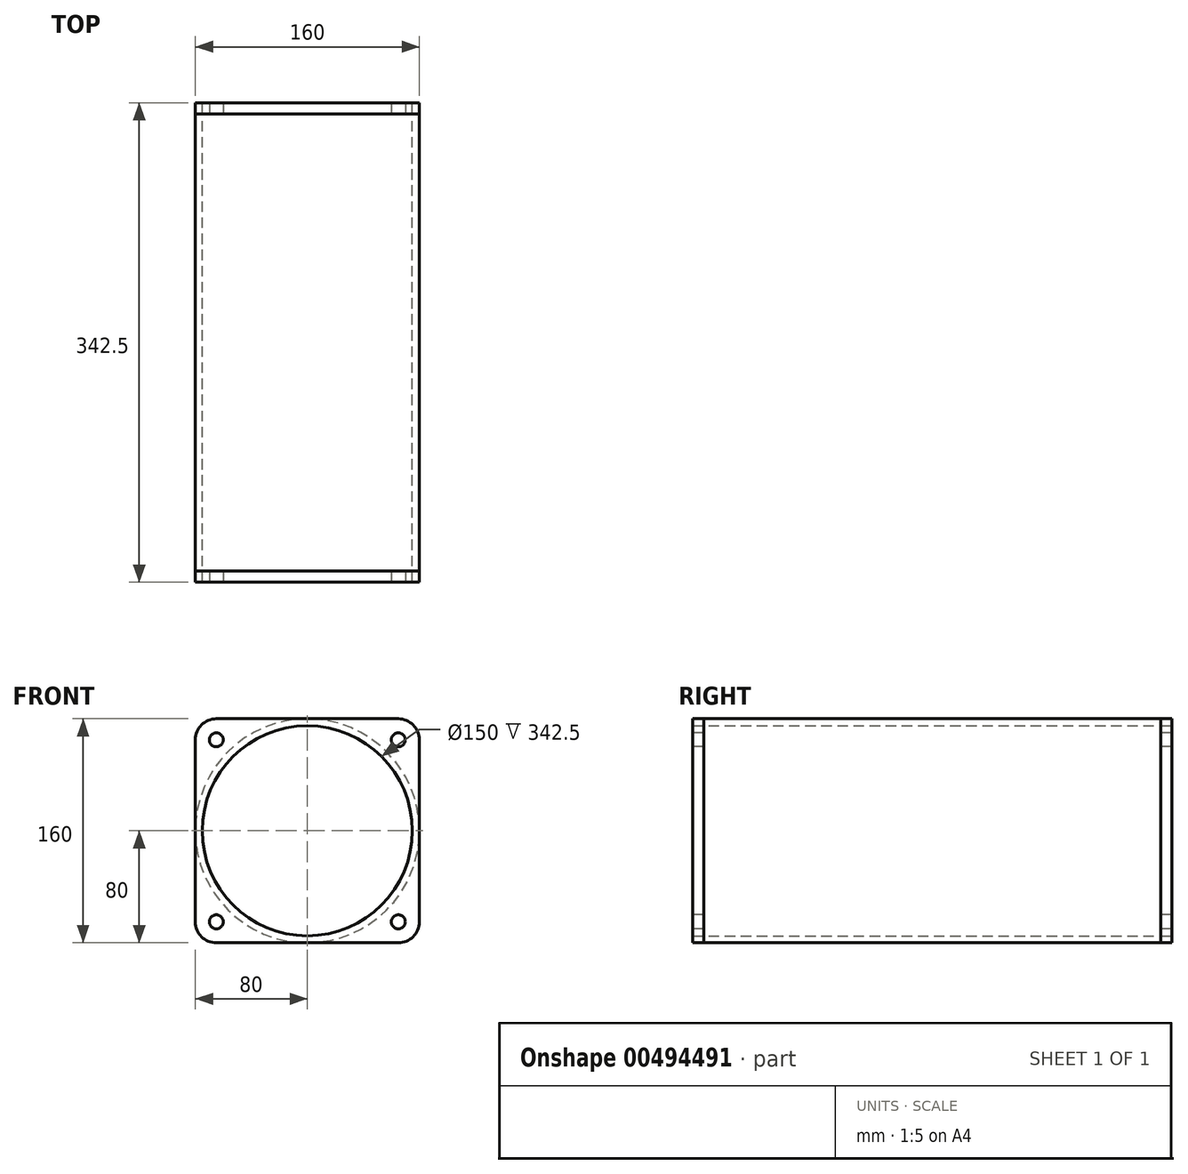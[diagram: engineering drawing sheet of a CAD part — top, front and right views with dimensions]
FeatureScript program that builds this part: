
annotation { "Feature Type Name" : "Feature", "Feature Type Description" : "" }
export const myFeature = defineFeature(function(context is Context, id is Id, definition is map)
    precondition{}
    {
        {
            var Q0;
            Q0=qCreatedBy(makeId("Front.planeOp"),FACE);
            var sketch = newSketch(context, id + "F0", { "sketchPlane" : qUnion([Q0])});
            skLineSegment(sketch, "E0.bottom", {"start": v(80, -80) * mm, "end": v(-80, -80) * mm});
            skLineSegment(sketch, "E0.top", {"start": v(80, 80) * mm, "end": v(-80, 80) * mm});
            skLineSegment(sketch, "E0.left", {"start": v(80, -80) * mm, "end": v(80, 80) * mm});
            skLineSegment(sketch, "E0.right", {"start": v(-80, -80) * mm, "end": v(-80, 80) * mm});
            skPoint(sketch, "E0.middle", {"position": v(0, 0) * mm});
            skCircle(sketch, "E1", {"center": v(0, 0) * mm, "radius": 75 * mm});
            skSolve(sketch);
        }
        {
            var Q0;
            Q0=makeQuery(id+"F0.imprint","IMPRINT",FACE,{"disambiguationData":[TD([[makeQuery(id+"F0.imprint","IMPRINT",EDGE,{"derivedFrom":sQuery(id+"F0.wireOp",EDGE,"E1")}),1.0]])]});
            extrude(context, id + "F1", {"entities" : qUnion([Q0]), "endBound" : BoundingType.SYMMETRIC, "depth" : 342.5 * mm});
        }
        {
            var Q0;
            Q0=makeQuery(id+"F1.opExtrude","CAP_FACE",FACE,{"disambiguationData":[OSD([sQuery(id+"F0.wireOp",EDGE,"E1")])],"isStart":false});
            var Q1;
            Q1=makeQuery(id+"F1.opExtrude","CAP_FACE",FACE,{"disambiguationData":[OSD([sQuery(id+"F0.wireOp",EDGE,"E1")])],"isStart":true});
            shell(context, id + "F2", {"entities" : qUnion([Q0, Q1]), "thickness" : 5 * mm, "oppositeDirection" : true});
        }
        {
            var Q0;
            Q0 = qSketchRegion(id + "F0", true);
            extrude(context, id + "F3", {"entities" : qUnion([Q0]), "operationType" : NewBodyOperationType.ADD, "oppositeDirection" : true, "depth" : (342.5 / 2) * mm, "hasSecondDirection" : true, "secondDirectionOppositeDirection" : true, "secondDirectionDepth" : (342.5 / 2 - 8) * mm});
        }
        {
            var Q0;
            Q0 = qSketchRegion(id + "F0", true);
            extrude(context, id + "F4", {"entities" : qUnion([Q0]), "operationType" : NewBodyOperationType.ADD, "depth" : (342.5 / 2) * mm, "hasSecondDirection" : true, "secondDirectionOppositeDirection" : false, "secondDirectionDepth" : (342.5 / 2 - 8) * mm});
        }
        {
            var Q0;
            {var subQ0=sQuery(id+"F0.wireOp",EDGE,"E1");Q0=makeQuery(id+"F4.boolean.opBoolean","MERGE",FACE,{"derivedFrom":[makeQuery(id+"F1.opExtrude","CAP_FACE",FACE,{"disambiguationData":[OSD([subQ0])],"isStart":false}),makeQuery(id+"F4.opExtrude","CAP_FACE",FACE,{"disambiguationData":[OSD([sQuery(id+"F0.wireOp",EDGE,"E0.bottom"),sQuery(id+"F0.wireOp",EDGE,"E0.top"),sQuery(id+"F0.wireOp",EDGE,"E0.left"),sQuery(id+"F0.wireOp",EDGE,"E0.right"),subQ0])],"isStart":false})]});}
            var sketch = newSketch(context, id + "F5", { "sketchPlane" : qUnion([Q0])});
            skCircle(sketch, "E2", {"center": v(-65, 65) * mm, "radius": 5 * mm});
            skCircle(sketch, "E3", {"center": v(65, 65) * mm, "radius": 5 * mm});
            skCircle(sketch, "E4", {"center": v(65, -65) * mm, "radius": 5 * mm});
            skCircle(sketch, "E5", {"center": v(-65, -65) * mm, "radius": 5 * mm});
            skSolve(sketch);
        }
        {
            var Q0;
            Q0=makeQuery(id+"F5.imprint","IMPRINT",FACE,{"disambiguationData":[TD([[makeQuery(id+"F5.imprint","IMPRINT",EDGE,{"derivedFrom":sQuery(id+"F5.wireOp",EDGE,"E2")}),1.0]])]});
            var Q1;
            Q1=makeQuery(id+"F5.imprint","IMPRINT",FACE,{"disambiguationData":[TD([[makeQuery(id+"F5.imprint","IMPRINT",EDGE,{"derivedFrom":sQuery(id+"F5.wireOp",EDGE,"E3")}),1.0]])]});
            var Q2;
            Q2=makeQuery(id+"F5.imprint","IMPRINT",FACE,{"disambiguationData":[TD([[makeQuery(id+"F5.imprint","IMPRINT",EDGE,{"derivedFrom":sQuery(id+"F5.wireOp",EDGE,"E4")}),1.0]])]});
            var Q3;
            Q3=makeQuery(id+"F5.imprint","IMPRINT",FACE,{"disambiguationData":[TD([[makeQuery(id+"F5.imprint","IMPRINT",EDGE,{"derivedFrom":sQuery(id+"F5.wireOp",EDGE,"E5")}),1.0]])]});
            extrude(context, id + "F6", {"entities" : qUnion([Q0, Q1, Q2, Q3]), "operationType" : NewBodyOperationType.REMOVE, "endBound" : BoundingType.THROUGH_ALL, "oppositeDirection" : true, "depth" : 25 * mm});
        }
        {
            var Q0;
            Q0=makeQuery(id+"F4.opExtrude","SWEPT_EDGE",EDGE,{"disambiguationData":[OSD([sQuery(id+"F0.wireOp",EDGE,"E0.top"),sQuery(id+"F0.wireOp",EDGE,"E0.right")])]});
            var Q1;
            Q1=makeQuery(id+"F4.opExtrude","SWEPT_EDGE",EDGE,{"disambiguationData":[OSD([sQuery(id+"F0.wireOp",EDGE,"E0.top"),sQuery(id+"F0.wireOp",EDGE,"E0.left")])]});
            var Q2;
            Q2=makeQuery(id+"F4.opExtrude","SWEPT_EDGE",EDGE,{"disambiguationData":[OSD([sQuery(id+"F0.wireOp",EDGE,"E0.bottom"),sQuery(id+"F0.wireOp",EDGE,"E0.left")])]});
            var Q3;
            Q3=makeQuery(id+"F4.opExtrude","SWEPT_EDGE",EDGE,{"disambiguationData":[OSD([sQuery(id+"F0.wireOp",EDGE,"E0.bottom"),sQuery(id+"F0.wireOp",EDGE,"E0.right")])]});
            var Q4;
            Q4=makeQuery(id+"F3.opExtrude","SWEPT_EDGE",EDGE,{"disambiguationData":[OSD([sQuery(id+"F0.wireOp",EDGE,"E0.bottom"),sQuery(id+"F0.wireOp",EDGE,"E0.right")])]});
            var Q5;
            Q5=makeQuery(id+"F3.opExtrude","SWEPT_EDGE",EDGE,{"disambiguationData":[OSD([sQuery(id+"F0.wireOp",EDGE,"E0.top"),sQuery(id+"F0.wireOp",EDGE,"E0.right")])]});
            var Q6;
            Q6=makeQuery(id+"F3.opExtrude","SWEPT_EDGE",EDGE,{"disambiguationData":[OSD([sQuery(id+"F0.wireOp",EDGE,"E0.top"),sQuery(id+"F0.wireOp",EDGE,"E0.left")])]});
            var Q7;
            Q7=makeQuery(id+"F3.opExtrude","SWEPT_EDGE",EDGE,{"disambiguationData":[OSD([sQuery(id+"F0.wireOp",EDGE,"E0.bottom"),sQuery(id+"F0.wireOp",EDGE,"E0.left")])]});
            fillet(context, id + "F7", {"entities" : qUnion([Q0, Q1, Q2, Q3, Q4, Q5, Q6, Q7]), "radius" : 15 * mm, "tangentPropagation" : true, "allowEdgeOverflow" : false});
        }
    });
